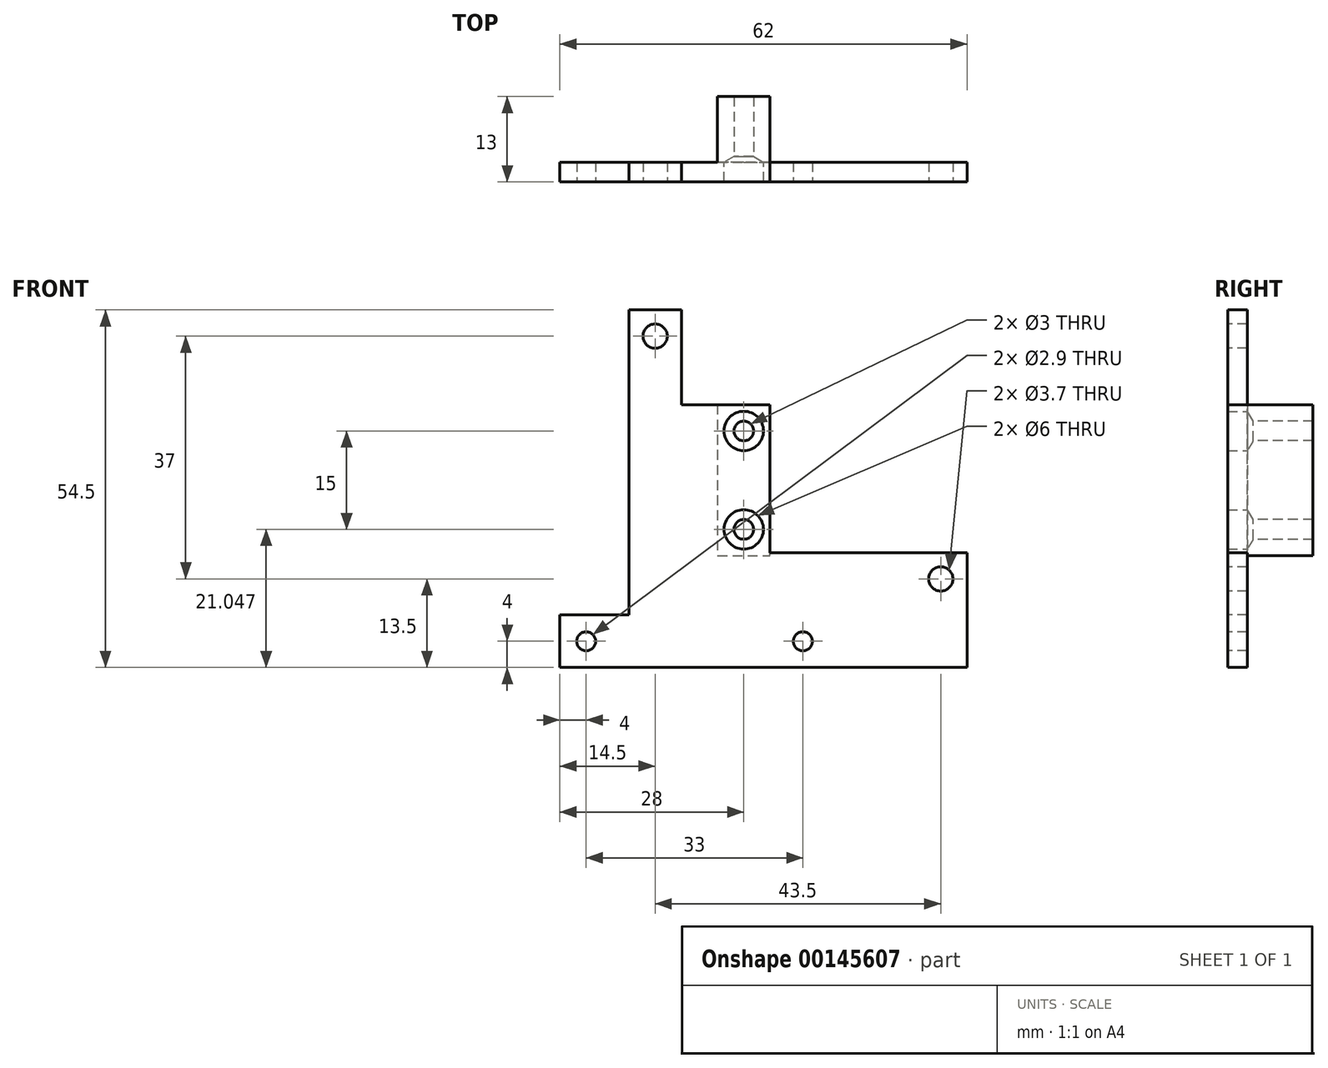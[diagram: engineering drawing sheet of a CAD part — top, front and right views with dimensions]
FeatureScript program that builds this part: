
annotation { "Feature Type Name" : "Feature", "Feature Type Description" : "" }
export const myFeature = defineFeature(function(context is Context, id is Id, definition is map)
    precondition{}
    {
        {
            var Q0;
            Q0=qCreatedBy(makeId("Front.planeOp"),FACE);
            var sketch = newSketch(context, id + "F0", { "sketchPlane" : qUnion([Q0])});
            skLineSegment(sketch, "E0", {"start": v(10, 53.53) * mm, "end": v(10, -53.24) * mm, "construction": true});
            skCircle(sketch, "E1", {"center": v(-6.5, -1) * mm, "radius": 1.45 * mm});
            skCircle(sketch, "E2", {"center": v(26.5, -1) * mm, "radius": 1.45 * mm});
            skCircle(sketch, "E3", {"center": v(4, 45.5) * mm, "radius": 1.85 * mm});
            skCircle(sketch, "E4", {"center": v(47.5, 8.5) * mm, "radius": 1.85 * mm});
            skLineSegment(sketch, "E5.bottom", {"start": v(2.5, 31.05) * mm, "end": v(17.5, 31.05) * mm, "construction": true});
            skLineSegment(sketch, "E5.top", {"start": v(2.5, 16.05) * mm, "end": v(17.5, 16.05) * mm, "construction": true});
            skLineSegment(sketch, "E5.left", {"start": v(2.5, 31.05) * mm, "end": v(2.5, 16.05) * mm, "construction": true});
            skLineSegment(sketch, "E5.right", {"start": v(17.5, 31.05) * mm, "end": v(17.5, 16.05) * mm, "construction": true});
            skCircle(sketch, "E6", {"center": v(17.5, 31.05) * mm, "radius": 1.5 * mm});
            skCircle(sketch, "E7", {"center": v(17.5, 16.05) * mm, "radius": 1.5 * mm});
            skPoint(sketch, "E8", {"position": v(10, 31.05) * mm});
            skLineSegment(sketch, "E9", {"start": v(51.5, -5) * mm, "end": v(51.5, 12.5) * mm});
            skLineSegment(sketch, "E10", {"start": v(51.5, 12.5) * mm, "end": v(21.5, 12.5) * mm});
            skLineSegment(sketch, "E11", {"start": v(21.5, 12.5) * mm, "end": v(21.5, 35.05) * mm});
            skLineSegment(sketch, "E12", {"start": v(21.5, 35.05) * mm, "end": v(8, 35.05) * mm});
            skLineSegment(sketch, "E13", {"start": v(8, 35.05) * mm, "end": v(8, 49.5) * mm});
            skLineSegment(sketch, "E14", {"start": v(8, 49.5) * mm, "end": v(0, 49.5) * mm});
            skLineSegment(sketch, "E15", {"start": v(0, 3) * mm, "end": v(-10.5, 3) * mm});
            skLineSegment(sketch, "E16", {"start": v(51.5, -5) * mm, "end": v(-10.5, -5) * mm});
            skPoint(sketch, "E17", {"position": v(0, 3) * mm});
            skLineSegment(sketch, "E18", {"start": v(0, 3) * mm, "end": v(0, 49.5) * mm});
            skLineSegment(sketch, "E19", {"start": v(-10.5, -5) * mm, "end": v(-10.5, 3) * mm});
            skLineSegment(sketch, "E20", {"start": v(13.5, 35.05) * mm, "end": v(13.5, 12.05) * mm});
            skLineSegment(sketch, "E21", {"start": v(13.5, 12.05) * mm, "end": v(21.5, 12.05) * mm});
            skLineSegment(sketch, "E22", {"start": v(21.5, 12.05) * mm, "end": v(21.5, 12.5) * mm});
            skSolve(sketch);
        }
        {
            var Q0;
            Q0 = qSketchRegion(id + "F0", true);
            extrude(context, id + "F1", {"entities" : qUnion([Q0]), "oppositeDirection" : true, "depth" : 3 * mm, "offsetDistance" : 25 * mm});
        }
        {
            var Q0;
            Q0=makeQuery(id+"F0.imprint","IMPRINT",FACE,{"disambiguationData":[TD([[makeQuery(id+"F0.imprint","IMPRINT",EDGE,{"derivedFrom":sQuery(id+"F0.wireOp",EDGE,"E6")}),-1.0]])]});
            extrude(context, id + "F2", {"entities" : qUnion([Q0]), "operationType" : NewBodyOperationType.ADD, "oppositeDirection" : true, "depth" : 13 * mm, "offsetDistance" : 25 * mm});
        }
        {
            var Q0;
            Q0=sQuery(id+"F0.wireOp",VERTEX,"E6.center");
            var Q1;
            Q1=sQuery(id+"F0.wireOp",VERTEX,"E7.center");
            var Q2;
            Q2=makeQuery(id+"F1.opExtrude","SWEPT_BODY",BODY,{"disambiguationData":[OSD([sQuery(id+"F0.wireOp",EDGE,"E1"),sQuery(id+"F0.wireOp",EDGE,"E2"),sQuery(id+"F0.wireOp",EDGE,"E3"),sQuery(id+"F0.wireOp",EDGE,"E4"),sQuery(id+"F0.wireOp",EDGE,"E6"),sQuery(id+"F0.wireOp",EDGE,"E7"),sQuery(id+"F0.wireOp",EDGE,"E9"),sQuery(id+"F0.wireOp",EDGE,"E10"),sQuery(id+"F0.wireOp",EDGE,"E11"),sQuery(id+"F0.wireOp",EDGE,"E12"),sQuery(id+"F0.wireOp",EDGE,"E13"),sQuery(id+"F0.wireOp",EDGE,"E14"),sQuery(id+"F0.wireOp",EDGE,"E15"),sQuery(id+"F0.wireOp",EDGE,"E16"),sQuery(id+"F0.wireOp",EDGE,"E18"),sQuery(id+"F0.wireOp",EDGE,"E19")])]});
            hole(context, id + "F3", {"style" : HoleStyle.SIMPLE, "endStyle" : HoleEndStyle.BLIND, "holeDiameter" : 6 * mm, "holeDepth" : 3 * mm, "tappedDepth" : 12 * mm, "tapClearance" : 3, "locations" : qUnion([Q0, Q1]), "scope" : qUnion([Q2])});
        }
    });
